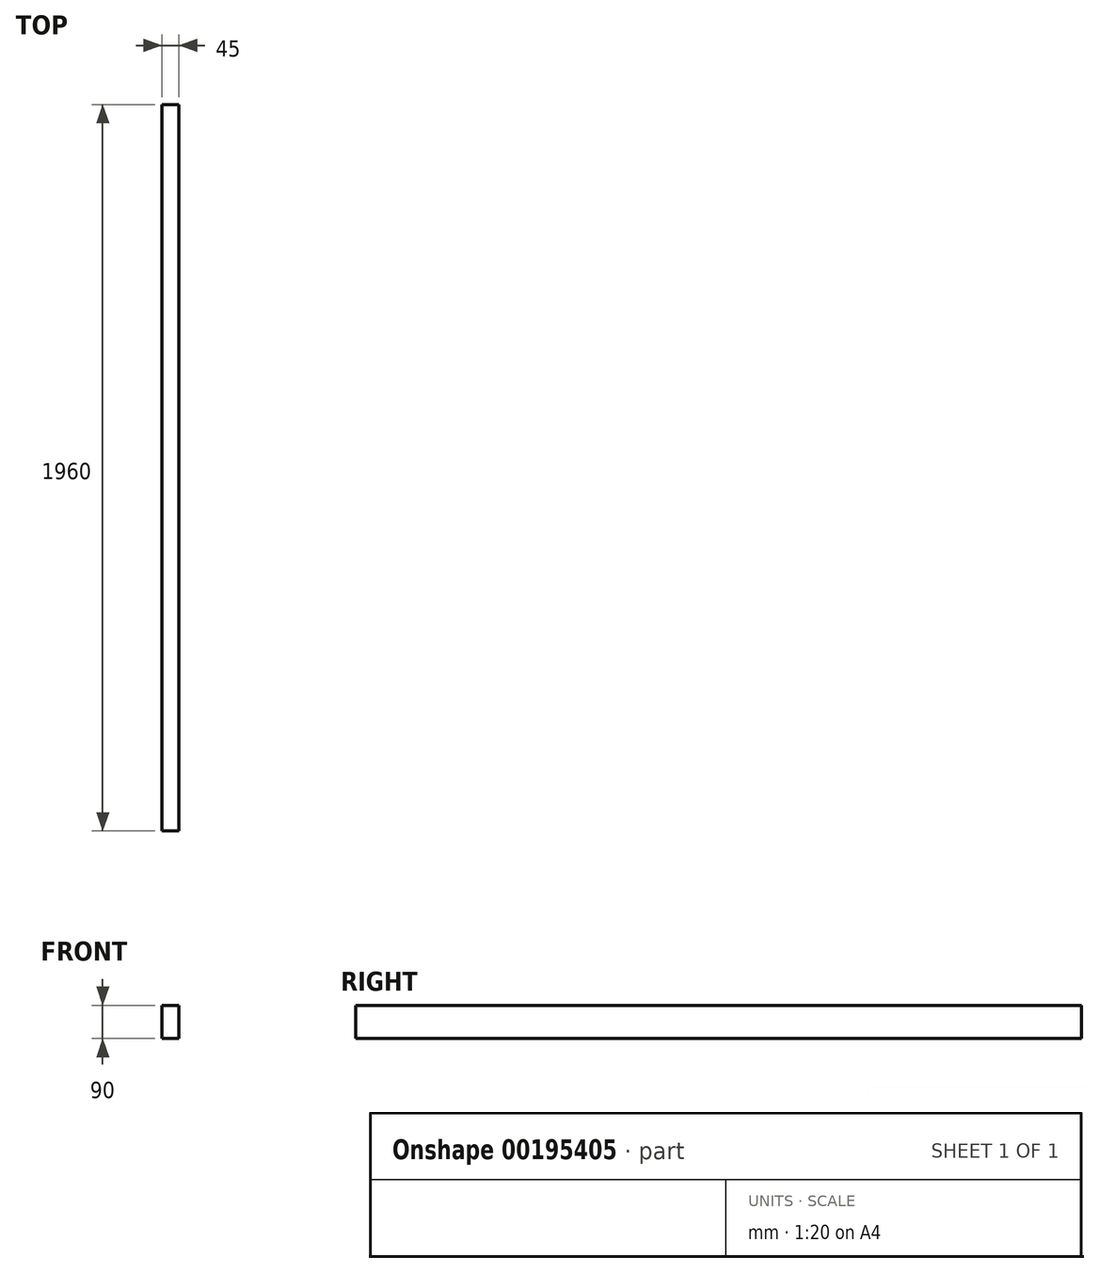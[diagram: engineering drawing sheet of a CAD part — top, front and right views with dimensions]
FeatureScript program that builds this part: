
annotation { "Feature Type Name" : "Feature", "Feature Type Description" : "" }
export const myFeature = defineFeature(function(context is Context, id is Id, definition is map)
    precondition{}
    {
        {
            var Q0;
            Q0=qCreatedBy(makeId("Right.planeOp"),FACE);
            var sketch = newSketch(context, id + "F0", { "sketchPlane" : qUnion([Q0])});
            skLineSegment(sketch, "E0.bottom", {"start": v(-980, 45) * mm, "end": v(980, 45) * mm});
            skLineSegment(sketch, "E0.top", {"start": v(-980, -45) * mm, "end": v(980, -45) * mm});
            skLineSegment(sketch, "E0.left", {"start": v(-980, 45) * mm, "end": v(-980, -45) * mm});
            skLineSegment(sketch, "E0.right", {"start": v(980, 45) * mm, "end": v(980, -45) * mm});
            skPoint(sketch, "E0.middle", {"position": v(0, 0) * mm});
            skSolve(sketch);
        }
        {
            var Q0;
            Q0 = qSketchRegion(id + "F0", true);
            extrude(context, id + "F1", {"entities" : qUnion([Q0]), "depth" : 45 * mm});
        }
    });
